# Revit family: Safety-Equipment_Metal-Railings_Omega-Industrial_4x4-Offset-Perimeter-Post
name_source: partatom
category: Balusters
units: mm (PartAtom-declared; Revit-internal decimal feet)

## family parameters
Always vertical = Yes
Classification Number = 23.30.80.17
Cut with Voids When Loaded = No
Shared = No

## types (1)
- Safety-Equipment_Metal-Railings_Omega-Industrial_4x4-Offset-Perimeter-Post
    Assembly Code = C2010400
    Base Material = Omega_1/2 in Steel
    Base Plate Depth = 0' - 10"
    Base Plate Width = 0' - 10"
    Description = Baluster Post as Specified in 05 52 00
    Expected Lifespan (Years) = 25
    Installation Phase = Industrial Safety Equipment
    Keynote = 41 67 19
    Maintenance Schedule (Months) = 0
    Manufacturer = Omega Industrial Products, Inc.
    Manufacturer Fax = 262-284-4199
    Manufacturer Website = https://www.omegaindl.com
    Model = As Specified in 05 52 00
    Post = Yes
    Post Cap Material = Omega_Black Plastic Bollard Cap
    Post Material = Omega_7 Ga. Steel
    Product Data = https://www.arcat.com
    Product Properties = https://www.omegaindl.com
    Revision = R0_06-2018
    Sales Information = https://www.omegaindl.com
    Send Message = https://www.omegaindl.com
    Specification = https://www.arcat.com
    URL = https://www.arcat.com
    Warranty Duration (Years) = 0

## geometry (parser evidence)
native form markers: Blend x38, Sweep x2
no freeform markers — native parametric forms only
